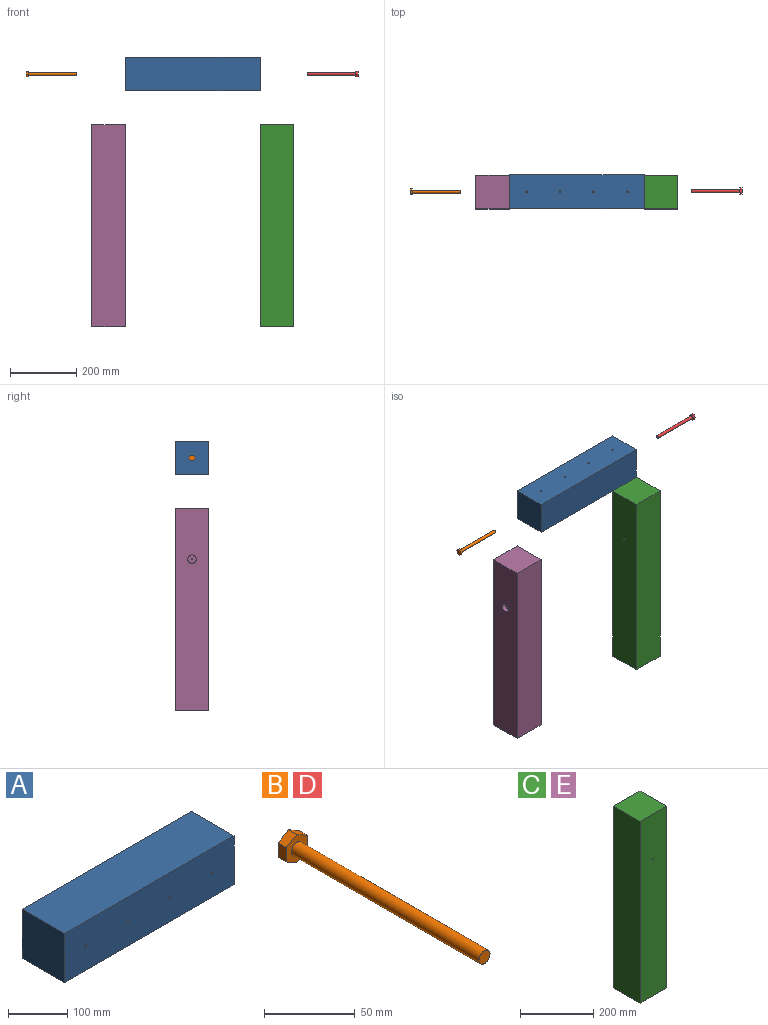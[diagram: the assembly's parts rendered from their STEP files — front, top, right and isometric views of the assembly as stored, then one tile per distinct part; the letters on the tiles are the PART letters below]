
ASSEMBLY  parts=5 mates=2
PART A: 18 faces, bbox 406.4x101.6x101.6 mm
  f0: plane 406.4x101.6mm, normal (0,0,1), area 41290.2mm2, adj f1,f3,f4,f5
  f1: plane 101.6x101.6mm, normal (-1,0,0), area 10322.6mm2, adj f0,f2,f4,f5
  f2: plane 406.4x101.6mm, normal (0,0,-1), area 41290.2mm2, adj f1,f3,f4,f5
  f3: plane 101.6x101.6mm, normal (1,0,0), area 10322.6mm2, adj f0,f2,f4,f5
  f4: plane 406.4x101.6mm, normal (0,-1,0), area 41219mm2, adj f0,f1,f2,f3,f6,f9,f12,f15
  f5: plane 406.4x101.6mm, normal (0,1,0), area 39263.4mm2, adj f0,f1,f2,f3,f8,f11,f14,f17
  f6: cylinder r=2.38mm len=88.9mm, axis (0,1,0), area 1330.1mm2, adj f4,f7
  f7: plane 25.4x25.4mm, normal (0,1,0), area 488.9mm2, adj f6,f8
  f8: cylinder r=12.7mm len=25.4mm, axis (0,1,0), area 1013.4mm2, adj f5,f7
  f9: cylinder r=2.38mm len=88.9mm, axis (0,1,0), area 1330.1mm2, adj f4,f10
  f10: plane 25.4x25.4mm, normal (0,1,0), area 488.9mm2, adj f9,f11
  f11: cylinder r=12.7mm len=25.4mm, axis (0,1,0), area 1013.4mm2, adj f5,f10
  f12: cylinder r=2.38mm len=88.9mm, axis (0,1,0), area 1330.1mm2, adj f4,f13
  f13: plane 25.4x25.4mm, normal (0,1,0), area 488.9mm2, adj f12,f14
  f14: cylinder r=12.7mm len=25.4mm, axis (0,1,0), area 1013.4mm2, adj f5,f13
  f15: cylinder r=2.38mm len=88.9mm, axis (0,1,0), area 1330.1mm2, adj f4,f16
  f16: plane 25.4x25.4mm, normal (0,1,0), area 488.9mm2, adj f15,f17
  f17: cylinder r=12.7mm len=25.4mm, axis (0,1,0), area 1013.4mm2, adj f5,f16
PART B: 10 faces, bbox 16.6x152.4x19.2 mm
  f0: plane 8.3x6.35mm, normal (0.5,0,0.87), area 60.9mm2, adj f1,f5,f6,f7
  f1: plane 8.3x6.35mm, normal (-0.5,0,0.87), area 60.9mm2, adj f0,f2,f6,f7
  f2: plane 9.59x6.35mm, normal (-1,0,0), area 60.9mm2, adj f1,f3,f6,f7
  f3: plane 8.3x6.35mm, normal (-0.5,0,-0.87), area 60.9mm2, adj f2,f4,f6,f7
  f4: plane 8.3x6.35mm, normal (0.5,0,-0.87), area 60.9mm2, adj f3,f5,f6,f7
  f5: plane 9.59x6.35mm, normal (1,0,0), area 60.9mm2, adj f0,f4,f6,f7
  f6: plane 19.17x16.6mm, normal (0,-1,0), area 180.5mm2, adj f0,f1,f2,f3,f4,f5,f8
  f7: plane 19.17x16.6mm, normal (0,1,0), area 238.7mm2, adj f0,f1,f2,f3,f4,f5
  f8: cylinder r=4.3mm len=146.05mm, axis (0,1,0), area 3950.4mm2, adj f6,f9
  f9: plane 8.61x8.61mm, normal (0,-1,0), area 58.2mm2, adj f8
PART C: 9 faces, bbox 101.6x101.6x609.6 mm
  f0: plane 101.6x101.6mm, normal (0,0,1), area 10322.6mm2, adj f1,f3,f4,f5
  f1: plane 609.6x101.6mm, normal (-1,0,0), area 61935.4mm2, adj f0,f2,f4,f5
  f2: plane 101.6x101.6mm, normal (0,0,-1), area 10322.6mm2, adj f1,f3,f4,f5
  f3: plane 609.6x101.6mm, normal (1,0,0), area 61935.4mm2, adj f0,f2,f4,f5
  f4: plane 609.6x101.6mm, normal (0,-1,0), area 61917.5mm2, adj f0,f1,f2,f3,f6
  f5: plane 609.6x101.6mm, normal (0,1,0), area 61428.7mm2, adj f0,f1,f2,f3,f8
  f6: cylinder r=2.38mm len=88.9mm, axis (0,1,0), area 1330.1mm2, adj f4,f7
  f7: plane 25.4x25.4mm, normal (0,1,0), area 488.9mm2, adj f6,f8
  f8: cylinder r=12.7mm len=25.4mm, axis (0,1,0), area 1013.4mm2, adj f5,f7
PART D: same geometry as B
PART E: same geometry as C
PLACE A rot(axis=(-1,0,0),90deg) t=(-350.37,-366.85,34.74)mm
PLACE B rot(axis=(-0.58,0.58,0.58),120deg) t=(-853.29,-366.85,85.54)mm
PLACE C rot(axis=(0,0,-1),90deg) t=(-45.57,-534.27,-246.12)mm
PLACE D rot(axis=(0.58,0.58,-0.58),120deg) t=(147.48,-364.91,85.54)mm
PLACE E rot(axis=(0,0,1),90deg) t=(-655.17,-199.43,-246.12)mm
MATE planar E.f6 <-> A.f1  axis (1,0,0) through (-553.57,-366.85,-219.26)mm
MATE planar C.f6 <-> A.f3  axis (-1,0,0) through (-147.17,-366.85,-219.26)mm
